# Revit family: Building-IEC309Connections-GEWISS-67IB-INTERLOCKED-SOCKET-OUTLETS_IP67_WITHOUT_BOTTOM_MOD
name_source: partatom
category: Apparecchi elettrici
revit_build: Autodesk Revit 2016 (Build: 20161004_0715(x64)
units: mm (PartAtom-declared; Revit-internal decimal feet)

## family parameters
Condiviso = No
Host = Muro
Mantenere orientamento annotazione = Sì
Numero OmniClass = 23.80.50.14
Punto di calcolo locali = No
Quota connettore circolare = Usa diametro
Sempre verticale = Sì
Taglio con vuoti quando caricato = No
Tipo di parte = Normale
Titolo OmniClass = Plug Connectors

## types (18) — shared parameters
Altezza da terra = 1112 mm
Carico apparente = 0 VA
Catalogue = BUILDING
Catalogue Range = 67 IB
Circuit breaker = MT 6 kA C characteristic
Classificazione carico = Altro
Electrocod = 2222
Frequency = 50/60 Hz
Glow Wire Test = 850 °C
Glow wire test: = 850 °C
IDF = b83f6655-9841-43d4-b5be-f67be19551fa
IDT = a7f1347e-7fe6-401d-a8af-d935eaffb75e
IP degree = IP67
Immagine tipo = GW66157N.jpg
Numero poli = 3
Operating temperature: = -25 +40 °C
Potenza = 400 V
Presa = GW - ROSSO
Produttore = GEWISS S.p.A.
Protection = MCB
Rated frequency (Hz) = 50/60 Hz
SEO = Socket outlet
Shock resistance = IK08
Struttura = GEWISS - Grigio RAL - 7035
Struttura frontale = GEWISS -BLU
Technical sheet = https://www.gewiss.com
Thermo-pressure with ball = 125
Tipo Simbolo = PRESAINDSTAGNA : 3P
Typology = Vertical
URL = https://www.gewiss.com
Version file RFA = 18.0
Vetro = GEWISS - vetro
With back-mounting box = No
Working temperature = -25 ÷ +40 °C

## per-type parameters (varying)
| type | Colour | Colour: | Descrizione | EAN code | Modello | No. of poles | Number of poles | Rated current (A) | Rated current (In) | Rated voltage | Rated voltage: | Reference h |
| GW66158N - 3P+E16A400V V.INT.SOCK.O.NB.6H MT60 IP67 | Red | Red | 3P+E16A400V V.INT.SOCK.O.NB.6H MT60 IP67 | 8011564741034 | GW66158N | 3P+E | 3P+E | 16 | 16 | 380 - 415 V | 380 - 415 V | 6 |
| GW66162N - 2P+E32A110V V.INT.SOCK.O.NB.4H MT60 IP67 | Yellow | Yellow | 2P+E32A110V V.INT.SOCK.O.NB.4H MT60 IP67 | 8011564741058 | GW66162N | 2P+E | 3P+E | 32 | 32 | 100 - 130 V | 100 - 130 V | 4 |
| GW66168N - 2P+E32A400V V.INT.SOCK.O.NB.9H MT60 IP67 | Red | Red | 2P+E32A400V V.INT.SOCK.O.NB.9H MT60 IP67 | 8011564741119 | GW66168N | 2P+E | 3P+E | 32 | 32 | 380 - 415 V | 380 - 415 V | 9 |
| GW66156N - 3P+N+E16A230V V.IN.SOC.O.NB.9H MT60 IP67 | Blue | Blue | 3P+N+E16A230V V.IN.SOC.O.NB.9H MT60 IP67 | 8011564741010 | GW66156N | 3P+N+E | 3P+N+E | 16 | 16 | 200 - 250 V | 200 - 250 V | 9 |
| GW66155N - 3P+E16A230V V.INT.SOCK.O.NB.9H MT60 IP67 | Blue | Blue | 3P+E16A230V V.INT.SOCK.O.NB.9H MT60 IP67 | 8011564741003 | GW66155N | 3P+E | 3P+E | 16 | 16 | 200 - 250 V | 200 - 250 V | 9 |
| GW66152N - 3P+E16A110V V.INT.SOCK.O.NB.4H MT60 IP67 | Yellow | Yellow | 3P+E16A110V V.INT.SOCK.O.NB.4H MT60 IP67 | 8011564740976 | GW66152N | 3P+E | 3P+E | 16 | 16 | 100 - 130 V | 100 - 130 V | 4 |
| GW66163N - 3P+E32A110V V.INT.SOCK.O.NB.4H MT60 IP67 | Yellow | Yellow | 3P+E32A110V V.INT.SOCK.O.NB.4H MT60 IP67 | 8011564741065 | GW66163N | 3P+E | 3P+N+E | 32 | 32 | 100 - 130 V | 100 - 130 V | 4 |
| GW66166N - 3P+E32A230V V.INT.SOCK.O.NB.9H MT60 IP67 | Blue | Blue | 3P+E32A230V V.INT.SOCK.O.NB.9H MT60 IP67 | 8011564741096 | GW66166N | 3P+E | 3P+N+E | 32 | 32 | 200 - 250 V | 200 - 250 V | 9 |
| GW66154N - 2P+E16A230V V.INT.SOCK.O.NB.6H MT60 IP67 | Blue | Blue | 2P+E16A230V V.INT.SOCK.O.NB.6H MT60 IP67 | 8011564740990 | GW66154N | 2P+E | 2P+E | 16 | 16 | 200 - 250 V | 200 - 250 V | 6 |
| GW66159N - 3P+N+E16A400V V.IN.SOC.O.NB.6H MT60 IP67 | Red | Red | 3P+N+E16A400V V.IN.SOC.O.NB.6H MT60 IP67 | 8011564741041 | GW66159N | 3P+N+E | 3P+N+E | 16 | 16 | 380 - 415 V | 380 - 415 V | 6 |
| GW66153N - 3P+N+E16A110V V.IN.SOC.O.NB.4H MT60 IP67 | Yellow | Yellow | 3P+N+E16A110V V.IN.SOC.O.NB.4H MT60 IP67 | 8011564740983 | GW66153N | 3P+N+E | 3P+N+E | 16 | 16 | 100 - 130 V | 100 - 130 V | 4 |
| GW66169N - 3P+E32A400V V.INT.SOCK.O.NB.6H MT60 IP67 | Red | Red | 3P+E32A400V V.INT.SOCK.O.NB.6H MT60 IP67 | 8011564741126 | GW66169N | 3P+E | 3P+N+E | 32 | 32 | 380 - 415 V | 380 - 415 V | 6 |
| GW66157N - 2P+E16A400V V.INT.SOCK.O.NB.9H MT60 IP67 | Red | Red | 2P+E16A400V V.INT.SOCK.O.NB.9H MT60 IP67 | 8011564741027 | GW66157N | 2P+E | 2P+E | 16 | 16 | 380 - 415 V | 380 - 415 V | 9 |
| GW66167N - 3P+N+E32A230V V.IN.SOC.O.NB.9H MT60 IP67 | Blue | Blue | 3P+N+E32A230V V.IN.SOC.O.NB.9H MT60 IP67 | 8011564741102 | GW66167N | 3P+N+E | 2P+E | 32 | 32 | 200 - 250 V | 200 - 250 V | 9 |
| GW66165N - 2P+E32A230V V.INT.SOCK.O.NB.6H MT60 IP67 | Blue | Blue | 2P+E32A230V V.INT.SOCK.O.NB.6H MT60 IP67 | 8011564741089 | GW66165N | 2P+E | 3P+E | 32 | 32 | 200 - 250 V | 200 - 250 V | 6 |
| GW66170N - 3P+N+E32A400V V.IN.SOC.O.NB.6H MT60 IP67 | Red | Red | 3P+N+E32A400V V.IN.SOC.O.NB.6H MT60 IP67 | 8011564741133 | GW66170N | 3P+N+E | 2P+E | 32 | 32 | 380 - 415 V | 380 - 415 V | 6 |
| GW66151N - 2P+E16A110V V.INT.SOCK.O.NB.4H MT60 IP67 | Yellow | Yellow | 2P+E16A110V V.INT.SOCK.O.NB.4H MT60 IP67 | 8011564740969 | GW66151N | 2P+E | 2P+E | 16 | 16 | 100 - 130 V | 100 - 130 V | 4 |
| GW66164N - 3P+N+E32A110V V.IN.SOC.O.NB.4H MT60 IP67 | Yellow | Yellow | 3P+N+E32A110V V.IN.SOC.O.NB.4H MT60 IP67 | 8011564741072 | GW66164N | 3P+N+E | 2P+E | 32 | 32 | 100 - 130 V | 100 - 130 V | 4 |

note: source unit labels omitted for Thermo-pressure with ball — the stored unit's dimension contradicts the parameter name (converter mislabeling)

## geometry (parser evidence)
native form markers: Sweep x2
no freeform markers — native parametric forms only
